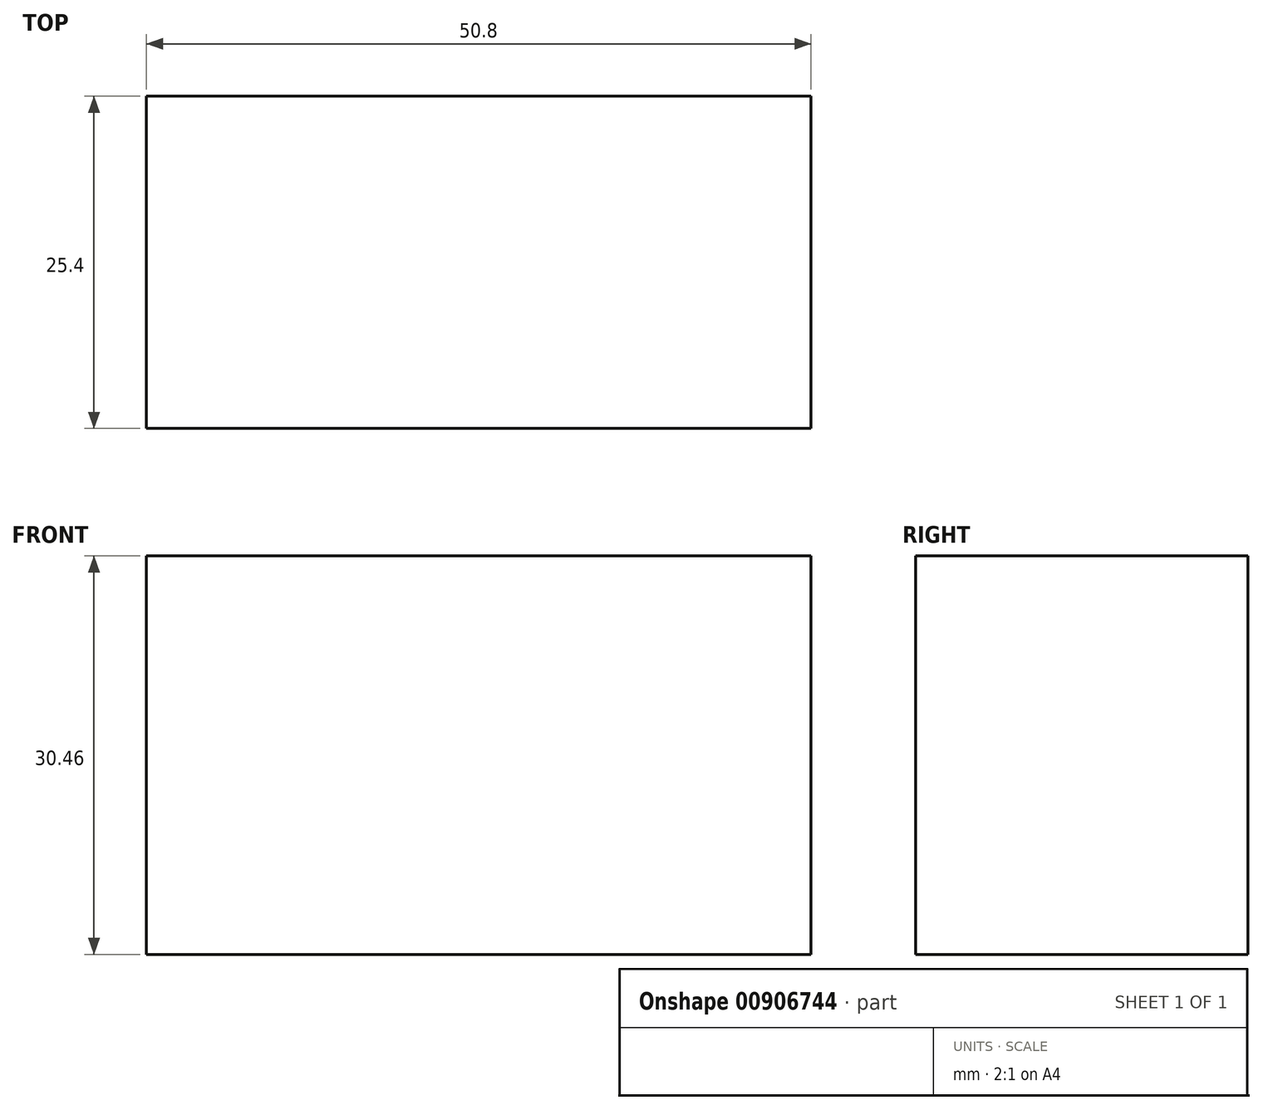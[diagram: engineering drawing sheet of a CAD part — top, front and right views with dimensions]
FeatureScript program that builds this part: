
annotation { "Feature Type Name" : "Feature", "Feature Type Description" : "" }
export const myFeature = defineFeature(function(context is Context, id is Id, definition is map)
    precondition{}
    {
        {
            var Q0;
            Q0=qCreatedBy(makeId("Front.planeOp"),FACE);
            var sketch = newSketch(context, id + "F0", { "sketchPlane" : qUnion([Q0])});
            skLineSegment(sketch, "E0.bottom", {"start": v(-35.87, 30.46) * mm, "end": v(14.93, 30.46) * mm});
            skLineSegment(sketch, "E0.top", {"start": v(-35.87, 0) * mm, "end": v(14.93, 0) * mm});
            skLineSegment(sketch, "E0.left", {"start": v(-35.87, 30.46) * mm, "end": v(-35.87, 0) * mm});
            skLineSegment(sketch, "E0.right", {"start": v(14.93, 30.46) * mm, "end": v(14.93, 0) * mm});
            skSolve(sketch);
        }
        {
            var Q0;
            Q0=makeQuery(id+"F0.imprint","IMPRINT",FACE,{"disambiguationData":[TD([[makeQuery(id+"F0.imprint","IMPRINT",EDGE,{"derivedFrom":sQuery(id+"F0.wireOp",EDGE,"E0.bottom")}),-1.0]])]});
            extrude(context, id + "F1", {"entities" : qUnion([Q0]), "depth" : 25.4 * mm, "offsetDistance" : 25.4 * mm});
        }
    });
